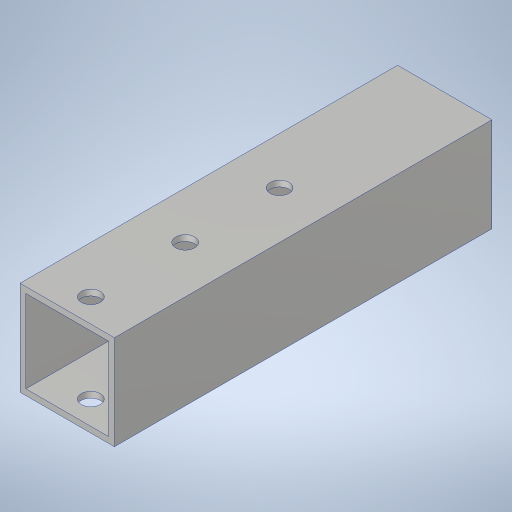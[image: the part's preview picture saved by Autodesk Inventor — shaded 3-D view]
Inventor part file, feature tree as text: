
AUTODESK INVENTOR PART (.ipt)
format: ipt  version: 2023.4 (Build 274418000, 418)  size: 224,256 bytes
history: native  units: in
note: dims shown in document units (in); Inventor stores cm internally (conversion verified against a paired STEP export)
features: sketch x2, extrude x1, hole x1
ambient origin geometry x8: Origin, YZ Plane, XZ Plane, XY Plane, X Axis, Y Axis, Z Axis, Center Point
bodies: Solid1 (feature_tree)
feature tree (4):
  extrude  "Extrusion1"  Depth=1.0in
  hole  "Hole1"  [1 undecoded]
  sketch  "Sketch1"  dims[d0=1.0in d1=1.0in]
  sketch  "Sketch2"  dims[d3=0.875in d4=0.875in d5=4.0in d6=0.0in d7=0.25in d8=1.0in d9=1.0in d10=0.201in d11=0.75in d12=0.385in d13=0.25in d14=0.5635in d15=1.0in d16=0.8108in]
note: 1 required parameter value undecoded (feature->parameter linkage not recoverable at this tier; creation-order binding heuristic only, values carry confidence <= 0.55)
